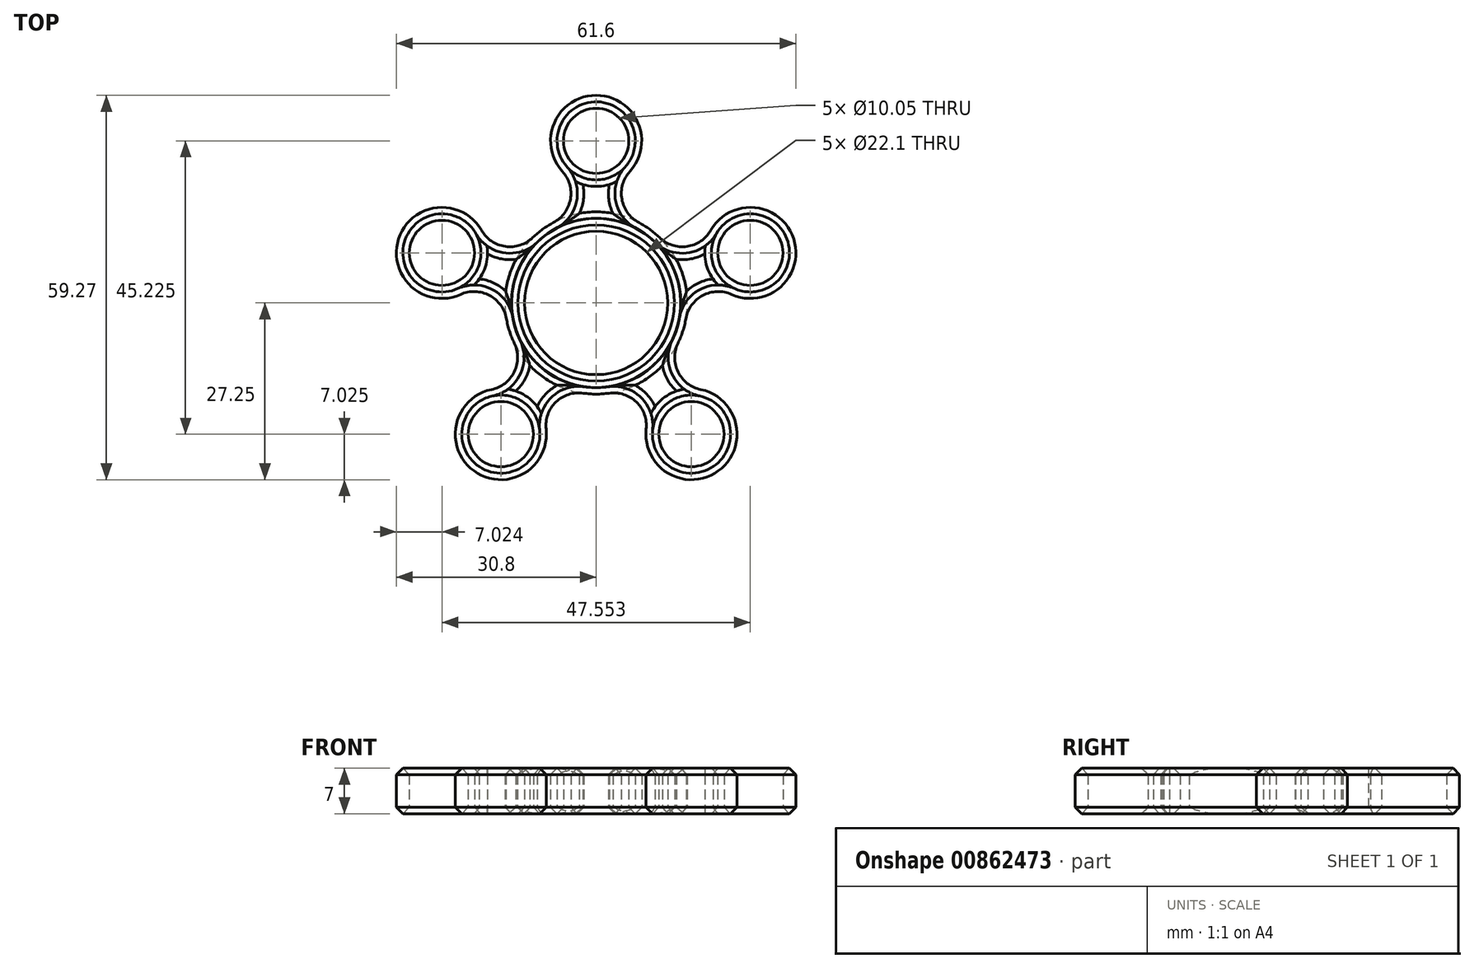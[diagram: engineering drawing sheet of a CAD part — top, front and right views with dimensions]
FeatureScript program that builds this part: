
annotation { "Feature Type Name" : "Feature", "Feature Type Description" : "" }
export const myFeature = defineFeature(function(context is Context, id is Id, definition is map)
    precondition{}
    {
        {
            var Q0;
            Q0=qCreatedBy(makeId("Top.planeOp"),FACE);
            var sketch = newSketch(context, id + "F0", { "sketchPlane" : qUnion([Q0])});
            skCircle(sketch, "E0", {"center": v(0, 0) * mm, "radius": 11.05 * mm});
            skCircle(sketch, "E1", {"center": v(0, 0) * mm, "radius": 14.05 * mm});
            skArc(sketch, "E2", {"start": v(-2.03, 18.27) * mm, "mid": v(0, 17.98) * mm, "end": v(2.03, 18.27) * mm});
            skCircle(sketch, "E3", {"center": v(0, 25) * mm, "radius": 5.03 * mm});
            skArc(sketch, "E4", {"start": v(-6.58, 12.41) * mm, "mid": v(-3.97, 16.01) * mm, "end": v(-5.2, 20.28) * mm});
            skArc(sketch, "E5.0", {"start": v(-2.6, 13.8) * mm, "mid": v(-1.95, 16) * mm, "end": v(-2.03, 18.27) * mm});
            skArc(sketch, "E6.MirrorCS", {"start": v(6.58, 12.41) * mm, "mid": v(3.97, 16.01) * mm, "end": v(5.2, 20.28) * mm});
            skArc(sketch, "E7.MirrorCS", {"start": v(2.6, 13.8) * mm, "mid": v(1.95, 16) * mm, "end": v(2.03, 18.27) * mm});
            skPoint(sketch, "E8.orphan", {"position": v(-7.82, 23.85) * mm});
            skPoint(sketch, "E9.orphan", {"position": v(7.82, 23.85) * mm});
            skArc(sketch, "E10.trimOffspring", {"start": v(5.2, 20.28) * mm, "mid": v(0, 32.03) * mm, "end": v(-5.2, 20.28) * mm});
            skPoint(sketch, "E11.start.orphan", {"position": v(-10.09, 9.92) * mm});
            skPoint(sketch, "E12.MirrorCS.start.orphan", {"position": v(10.09, 9.92) * mm});
            skSolve(sketch);
        }
        {
            var Q0;
            Q0=makeQuery(id+"F0.imprint","IMPRINT",FACE,{"disambiguationData":[TD([[makeQuery(id+"F0.imprint","IMPRINT",EDGE,{"derivedFrom":sQuery(id+"F0.wireOp",EDGE,"E2")}),1.0]])]});
            var Q1;
            Q1=makeQuery(id+"F0.imprint","IMPRINT",FACE,{"disambiguationData":[TD([[makeQuery(id+"F0.imprint","IMPRINT",EDGE,{"derivedFrom":sQuery(id+"F0.wireOp",EDGE,"E0")}),-1.0]])]});
            extrude(context, id + "F1", {"entities" : qUnion([Q0, Q1]), "depth" : 7 * mm, "offsetDistance" : 25 * mm});
        }
        {
            var Q0;
            Q0=makeQuery(id+"F1.opExtrude","CAP_EDGE",EDGE,{"disambiguationData":[OSD([sQuery(id+"F0.wireOp",EDGE,"E3")])],"isStart":false});
            var Q1;
            Q1=makeQuery(id+"F1.opExtrude","CAP_EDGE",EDGE,{"disambiguationData":[OSD([sQuery(id+"F0.wireOp",EDGE,"E0")])],"isStart":false});
            var Q2;
            Q2=makeQuery(id+"F1.opExtrude","CAP_EDGE",EDGE,{"disambiguationData":[OSD([sQuery(id+"F0.wireOp",EDGE,"E0")])],"isStart":true});
            var Q3;
            Q3=makeQuery(id+"F1.opExtrude","CAP_EDGE",EDGE,{"disambiguationData":[OSD([sQuery(id+"F0.wireOp",EDGE,"E3")])],"isStart":true});
            var Q4;
            Q4=makeQuery(id+"F1.opExtrude","CAP_EDGE",EDGE,{"disambiguationData":[OSD([sQuery(id+"F0.wireOp",EDGE,"E10.trimOffspring")])],"isStart":false});
            var Q5;
            {var subQ0=sQuery(id+"F0.wireOp",EDGE,"E1");Q5=makeQuery(id+"F1.opExtrude","CAP_EDGE",EDGE,{"disambiguationData":[OSD([subQ0]),TDD([makeQuery(id+"F0.imprint","IMPRINT",EDGE,{"disambiguationData":[TD([[makeQuery(id+"F0.imprint","INTERSECT",VERTEX,{"derivedFrom":[subQ0,sQuery(id+"F0.wireOp",EDGE,"E4")]}),-1.0]])],"derivedFrom":subQ0})])],"isStart":false});}
            var Q6;
            {var subQ0=sQuery(id+"F0.wireOp",EDGE,"E1");Q6=makeQuery(id+"F1.opExtrude","CAP_EDGE",EDGE,{"disambiguationData":[OSD([subQ0]),TDD([makeQuery(id+"F0.imprint","IMPRINT",EDGE,{"disambiguationData":[TD([[makeQuery(id+"F0.imprint","INTERSECT",VERTEX,{"derivedFrom":[subQ0,sQuery(id+"F0.wireOp",EDGE,"E4")]}),-1.0]])],"derivedFrom":subQ0})])],"isStart":true});}
            var Q7;
            Q7=makeQuery(id+"F1.opExtrude","CAP_EDGE",EDGE,{"disambiguationData":[OSD([sQuery(id+"F0.wireOp",EDGE,"E5.0")])],"isStart":false});
            var Q8;
            Q8=makeQuery(id+"F1.opExtrude","CAP_EDGE",EDGE,{"disambiguationData":[OSD([sQuery(id+"F0.wireOp",EDGE,"E7.MirrorCS")])],"isStart":false});
            var Q9;
            Q9=makeQuery(id+"F1.opExtrude","CAP_EDGE",EDGE,{"disambiguationData":[OSD([sQuery(id+"F0.wireOp",EDGE,"E7.MirrorCS")])],"isStart":true});
            var Q10;
            Q10=makeQuery(id+"F1.opExtrude","CAP_EDGE",EDGE,{"disambiguationData":[OSD([sQuery(id+"F0.wireOp",EDGE,"E5.0")])],"isStart":true});
            var Q11;
            {var subQ0=sQuery(id+"F0.wireOp",EDGE,"E1");Q11=makeQuery(id+"F1.opExtrude","CAP_EDGE",EDGE,{"disambiguationData":[OSD([subQ0]),TDD([makeQuery(id+"F0.imprint","IMPRINT",EDGE,{"disambiguationData":[TD([[makeQuery(id+"F0.imprint","INTERSECT",VERTEX,{"derivedFrom":[subQ0,sQuery(id+"F0.wireOp",EDGE,"E5.0")]}),1.0]])],"derivedFrom":subQ0})])],"isStart":true});}
            var Q12;
            {var subQ0=sQuery(id+"F0.wireOp",EDGE,"E1");Q12=makeQuery(id+"F1.opExtrude","CAP_EDGE",EDGE,{"disambiguationData":[OSD([subQ0]),TDD([makeQuery(id+"F0.imprint","IMPRINT",EDGE,{"disambiguationData":[TD([[makeQuery(id+"F0.imprint","INTERSECT",VERTEX,{"derivedFrom":[subQ0,sQuery(id+"F0.wireOp",EDGE,"E5.0")]}),1.0]])],"derivedFrom":subQ0})])],"isStart":false});}
            chamfer(context, id + "F2", {"entities" : qUnion([Q0, Q1, Q2, Q3, Q4, Q5, Q6, Q7, Q8, Q9, Q10, Q11, Q12]), "width" : 1 * mm, "tangentPropagation" : true});
        }
        {
            var Q0;
            Q0=makeQuery(id+"F1.opExtrude","SWEPT_BODY",BODY,{"disambiguationData":[OSD([sQuery(id+"F0.wireOp",EDGE,"E0"),sQuery(id+"F0.wireOp",EDGE,"E1"),sQuery(id+"F0.wireOp",EDGE,"E2"),sQuery(id+"F0.wireOp",EDGE,"E3"),sQuery(id+"F0.wireOp",EDGE,"E4"),sQuery(id+"F0.wireOp",EDGE,"E5.0"),sQuery(id+"F0.wireOp",EDGE,"E6.MirrorCS"),sQuery(id+"F0.wireOp",EDGE,"E7.MirrorCS"),sQuery(id+"F0.wireOp",EDGE,"E10.trimOffspring")])]});
            var Q1;
            {var subQ0=sQuery(id+"F0.wireOp",EDGE,"E0");Q1=makeQuery(id+"F2.opChamfer","BLEND_EDGE",EDGE,{"blendedFrom":[makeQuery(id+"F1.opExtrude","CAP_EDGE",EDGE,{"disambiguationData":[OSD([subQ0])],"isStart":false}),makeQuery(id+"F1.opExtrude","CAP_FACE",FACE,{"disambiguationData":[OSD([subQ0,sQuery(id+"F0.wireOp",EDGE,"E1"),sQuery(id+"F0.wireOp",EDGE,"E2"),sQuery(id+"F0.wireOp",EDGE,"E3"),sQuery(id+"F0.wireOp",EDGE,"E4"),sQuery(id+"F0.wireOp",EDGE,"E5.0"),sQuery(id+"F0.wireOp",EDGE,"E6.MirrorCS"),sQuery(id+"F0.wireOp",EDGE,"E7.MirrorCS"),sQuery(id+"F0.wireOp",EDGE,"E10.trimOffspring")])],"isStart":false})],"blendedInto":[makeQuery(id+"F1.opExtrude","CAP_FACE",FACE,{"disambiguationData":[OSD([subQ0,sQuery(id+"F0.wireOp",EDGE,"E1"),sQuery(id+"F0.wireOp",EDGE,"E2"),sQuery(id+"F0.wireOp",EDGE,"E3"),sQuery(id+"F0.wireOp",EDGE,"E4"),sQuery(id+"F0.wireOp",EDGE,"E5.0"),sQuery(id+"F0.wireOp",EDGE,"E6.MirrorCS"),sQuery(id+"F0.wireOp",EDGE,"E7.MirrorCS"),sQuery(id+"F0.wireOp",EDGE,"E10.trimOffspring")])],"isStart":false})]});}
            circularPattern(context, id + "F3", {"entities" : qUnion([Q0]), "axis" : qUnion([Q1]), "angle" : 360 * degree, "instanceCount" : 5, "equalSpace" : true});
        }
    });
